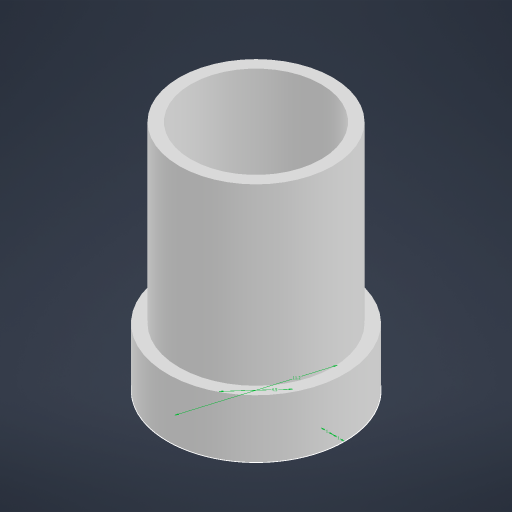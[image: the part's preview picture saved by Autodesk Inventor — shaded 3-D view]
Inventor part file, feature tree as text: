
AUTODESK INVENTOR PART (.ipt)
format: ipt  version: 2024.1 (Build 281209000, 209)  size: 179,712 bytes
history: native  units: mm
features: extrude x3, sketch x2
ambient origin geometry x8: Origin, YZ Plane, XZ Plane, XY Plane, X Axis, Y Axis, Z Axis, Center Point
bodies: Solid1 (feature_tree)
feature tree (5):
  sketch  "Sketch1"  dims[d0=11.2mm d1=4.5mm]
  extrude  "Extrusion1"  Depth=4.5mm
  extrude  "Extrusion3"  Depth=15.0mm
  extrude  "Extrusion5"  Depth=5.0mm TaperAngle=0.0deg
  sketch  "Sketch4"  dims[d6=1.0mm d7=1.0mm d8=5.0mm d9=0.0mm d14=15.0mm d15=0.0mm d19=2.5mm d20=15.0mm d21=0.0mm]
